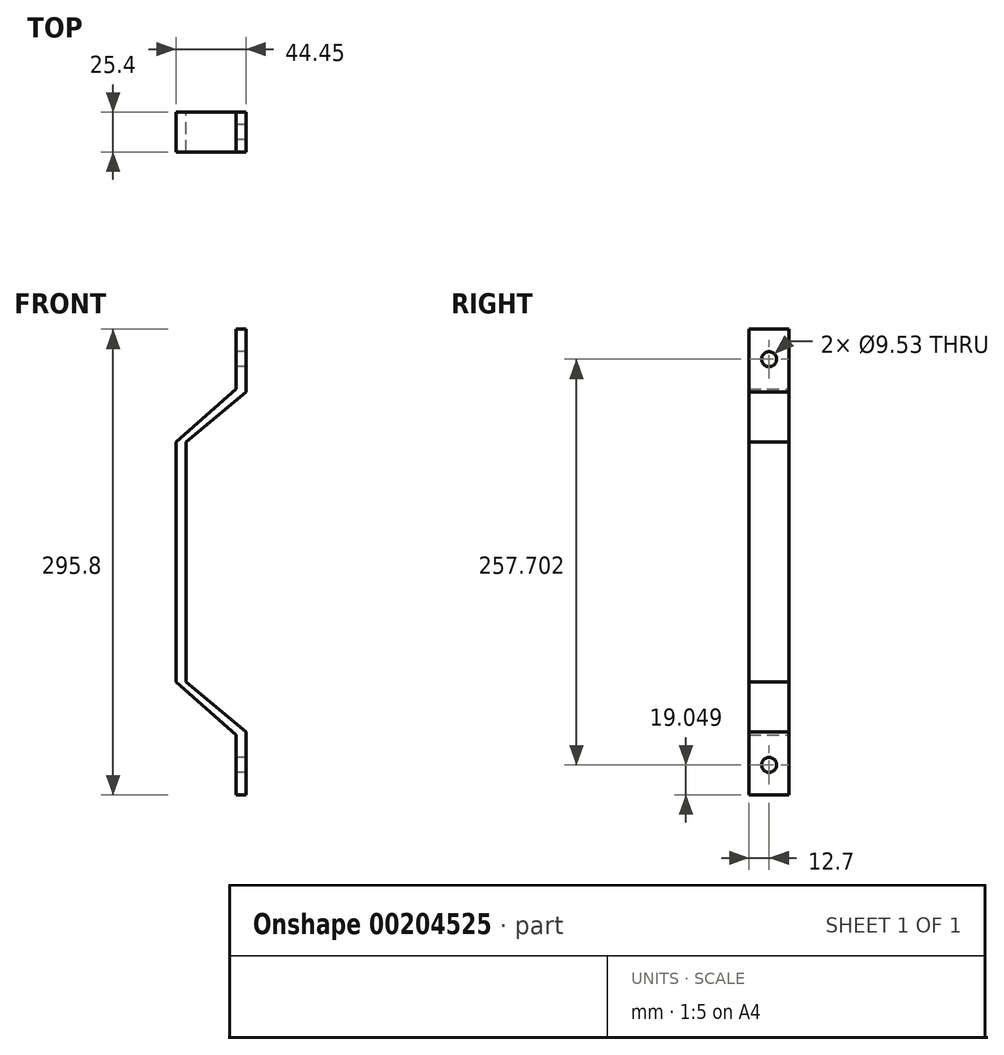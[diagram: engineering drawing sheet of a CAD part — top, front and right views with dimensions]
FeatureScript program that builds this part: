
annotation { "Feature Type Name" : "Feature", "Feature Type Description" : "" }
export const myFeature = defineFeature(function(context is Context, id is Id, definition is map)
    precondition{}
    {
        {
            var Q0;
            Q0=qCreatedBy(makeId("Front.planeOp"),FACE);
            var sketch = newSketch(context, id + "F0", { "sketchPlane" : qUnion([Q0])});
            skLineSegment(sketch, "E0", {"start": v(0, 0) * mm, "end": v(0, 76.2) * mm});
            skLineSegment(sketch, "E1", {"start": v(0, 76.2) * mm, "end": v(0, -76.2) * mm});
            skLineSegment(sketch, "E2", {"start": v(44.45, 107.95) * mm, "end": v(44.45, 147.9) * mm});
            skLineSegment(sketch, "E3", {"start": v(44.45, 147.9) * mm, "end": v(38.1, 147.9) * mm});
            skLineSegment(sketch, "E4", {"start": v(38.1, 147.9) * mm, "end": v(38.1, 109.8) * mm});
            skLineSegment(sketch, "E5.MirrorCS", {"start": v(38.1, -147.9) * mm, "end": v(38.1, -109.8) * mm});
            skLineSegment(sketch, "E6.MirrorCS", {"start": v(44.45, -147.9) * mm, "end": v(38.1, -147.9) * mm});
            skLineSegment(sketch, "E7.MirrorCS", {"start": v(44.45, -107.95) * mm, "end": v(44.45, -147.9) * mm});
            skLineSegment(sketch, "E8", {"start": v(0, -76.2) * mm, "end": v(38.1, -109.8) * mm});
            skLineSegment(sketch, "E9.0", {"start": v(6.35, 76.2) * mm, "end": v(6.35, -76.2) * mm});
            skLineSegment(sketch, "E10", {"start": v(6.35, -76.2) * mm, "end": v(44.45, -107.95) * mm});
            skLineSegment(sketch, "E11", {"start": v(6.35, 76.2) * mm, "end": v(44.45, 107.95) * mm});
            skLineSegment(sketch, "E12", {"start": v(0, 76.2) * mm, "end": v(38.1, 109.8) * mm});
            skPoint(sketch, "E13.MirrorCS.end.orphan", {"position": v(44.45, -107.95) * mm});
            skPoint(sketch, "E13.MirrorCS.start.orphan", {"position": v(38.1, -109.8) * mm});
            skSolve(sketch);
        }
        {
            var Q0;
            Q0=makeQuery(id+"F0.imprint","IMPRINT",FACE,{"disambiguationData":[TD([[makeQuery(id+"F0.imprint","IMPRINT",EDGE,{"derivedFrom":sQuery(id+"F0.wireOp",EDGE,"E2")}),1.0]])]});
            extrude(context, id + "F1", {"entities" : qUnion([Q0]), "depth" : 25.4 * mm});
        }
        {
            var Q0;
            Q0=makeQuery(id+"F1.opExtrude","SWEPT_FACE",FACE,{"disambiguationData":[OSD([sQuery(id+"F0.wireOp",EDGE,"E4")])]});
            var sketch = newSketch(context, id + "F2", { "sketchPlane" : qUnion([Q0])});
            skCircle(sketch, "E14", {"center": v(12.7, 128.85) * mm, "radius": 5.58 * mm});
            skPoint(sketch, "E14.centerSnap0", {"position": v(12.7, 147.9) * mm});
            skPoint(sketch, "E14.centerSnap1", {"position": v(0, 128.85) * mm});
            skCircle(sketch, "E15.MirrorC", {"center": v(12.7, -128.85) * mm, "radius": 5.58 * mm});
            skSolve(sketch);
        }
        {
            var Q0;
            Q0=sQuery(id+"F2.wireOp",VERTEX,"E14.center");
            var Q1;
            Q1=sQuery(id+"F2.wireOp",VERTEX,"E15.MirrorC.center");
            var Q2;
            Q2=makeQuery(id+"F1.opExtrude","SWEPT_BODY",BODY,{"disambiguationData":[OSD([sQuery(id+"F0.wireOp",EDGE,"E1"),sQuery(id+"F0.wireOp",EDGE,"E2"),sQuery(id+"F0.wireOp",EDGE,"E3"),sQuery(id+"F0.wireOp",EDGE,"E4"),sQuery(id+"F0.wireOp",EDGE,"E5.MirrorCS"),sQuery(id+"F0.wireOp",EDGE,"E6.MirrorCS"),sQuery(id+"F0.wireOp",EDGE,"E7.MirrorCS"),sQuery(id+"F0.wireOp",EDGE,"E8"),sQuery(id+"F0.wireOp",EDGE,"E9.0"),sQuery(id+"F0.wireOp",EDGE,"E10"),sQuery(id+"F0.wireOp",EDGE,"E11"),sQuery(id+"F0.wireOp",EDGE,"E12")])]});
            hole(context, id + "F3", {"style" : HoleStyle.SIMPLE, "endStyle" : HoleEndStyle.BLIND, "holeDiameter" : 9.52 * mm, "holeDepth" : 1524 * mm, "locations" : qUnion([Q0, Q1]), "scope" : qUnion([Q2])});
        }
    });
